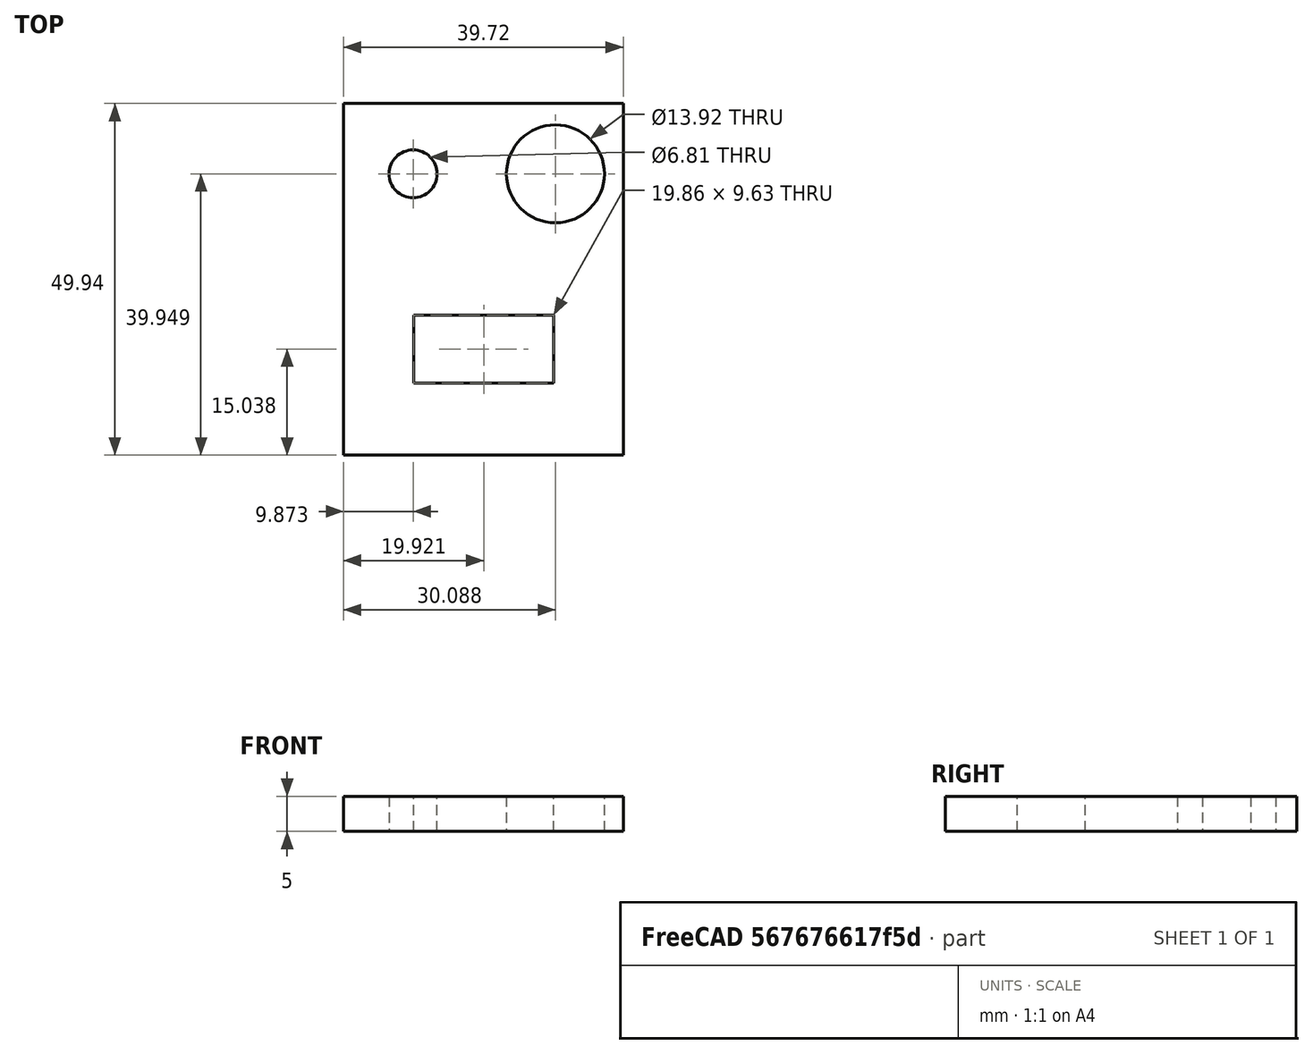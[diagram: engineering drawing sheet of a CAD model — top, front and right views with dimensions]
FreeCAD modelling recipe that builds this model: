
FCSTD DOCUMENT  (FreeCAD 0.20R29177 +233 (Git))
Label: cabeza-robot
License: Creative Commons Attribution-ShareAlike
LicenseURL: http://creativecommons.org/licenses/by-sa/4.0/
objects: Sketcher::SketchObject×1, Part::Extrusion×1
note: 2 computed .brp shape members not serialized (recipe doc carries the construction recipe); baked Part::Feature solids carry a one-line shape summary decoded from their .brp

FEATURE [Sketcher::SketchObject] Sketch
  FullyConstrained = false
  sketch-geometry (10):
    g0: LineSegment StartX=-20.0357 StartY=19.9168 StartZ=0 EndX=19.679 EndY=19.9168 EndZ=0
    g1: LineSegment StartX=19.679 StartY=19.9168 StartZ=0 EndX=19.679 EndY=-30.0238 EndZ=0
    g2: LineSegment StartX=19.679 StartY=-30.0238 StartZ=0 EndX=-20.0357 EndY=-30.0238 EndZ=0
    g3: LineSegment StartX=-20.0357 StartY=-30.0238 StartZ=0 EndX=-20.0357 EndY=19.9168 EndZ=0
    g4: LineSegment StartX=-10.0476 StartY=-10.1665 StartZ=0 EndX=9.80975 EndY=-10.1665 EndZ=0
    g5: LineSegment StartX=9.80975 StartY=-10.1665 StartZ=0 EndX=9.80975 EndY=-19.7979 EndZ=0
    g6: LineSegment StartX=9.80975 StartY=-19.7979 StartZ=0 EndX=-10.0476 EndY=-19.7979 EndZ=0
    g7: LineSegment StartX=-10.0476 StartY=-19.7979 StartZ=0 EndX=-10.0476 EndY=-10.1665 EndZ=0
    g8: Circle CenterX=-10.1665 CenterY=9.92866 CenterZ=0 NormalX=0 NormalY=0 NormalZ=1 AngleXU=0 Radius=3.40703
    g9: Circle CenterX=10.0476 CenterY=9.92866 CenterZ=0 NormalX=0 NormalY=0 NormalZ=1 AngleXU=0 Radius=6.9588
  constraints (16):
    c: Coincident(g0,g1)
    c: Coincident(g1,g2)
    c: Coincident(g2,g3)
    c: Coincident(g3,g0)
    c: Horizontal(g0)
    c: Horizontal(g2)
    c: Vertical(g1)
    c: Vertical(g3)
    c: Coincident(g4,g5)
    c: Coincident(g5,g6)
    c: Coincident(g6,g7)
    c: Coincident(g7,g4)
    c: Horizontal(g4)
    c: Horizontal(g6)
    c: Vertical(g5)
    c: Vertical(g7)
FEATURE [Part::Extrusion] Extrude
  Base = -> Sketch
  Dir = (0,0,1)
  DirMode = 2
  FaceMakerClass = Part::FaceMakerBullseye
  LengthFwd = 5
  LengthRev = 0
  Solid = true
  Symmetric = false
